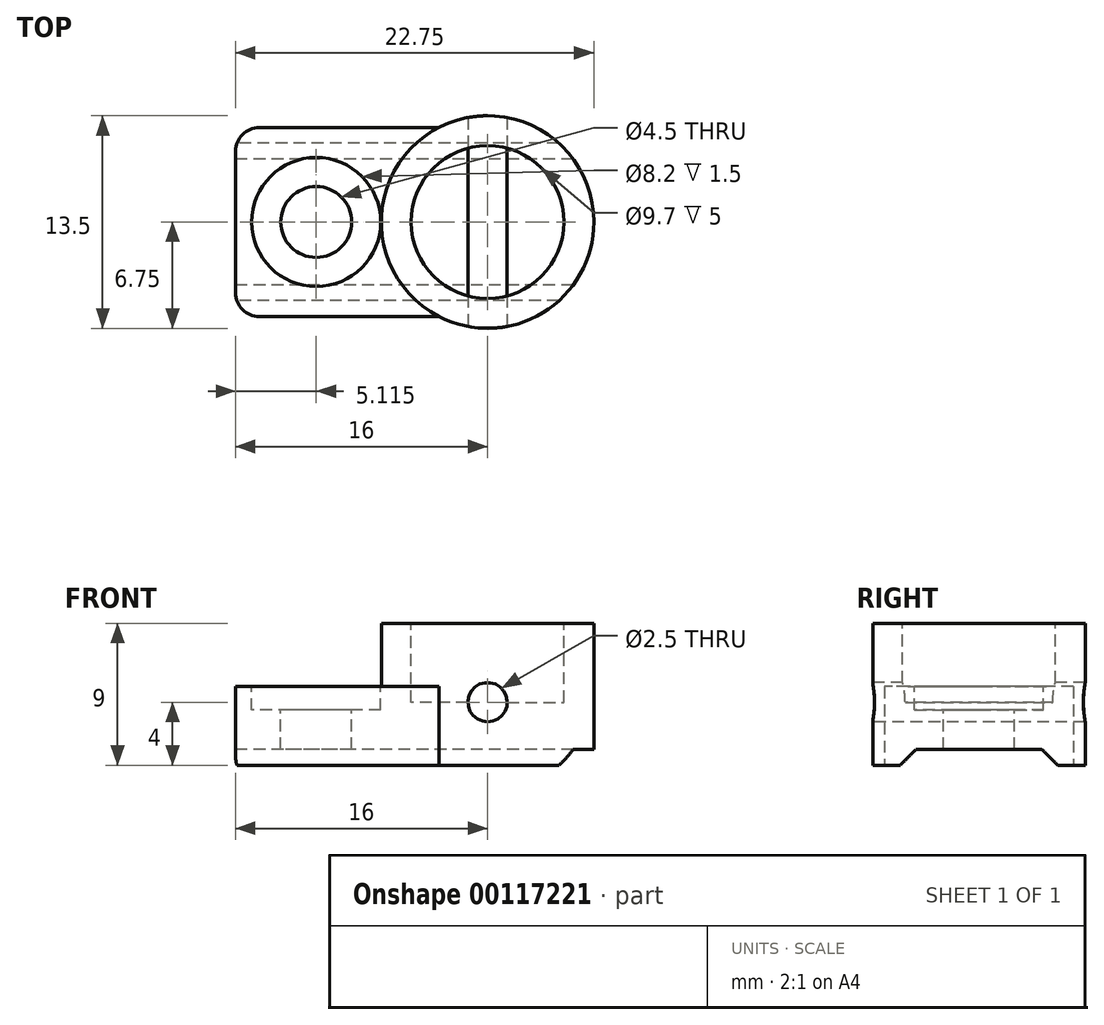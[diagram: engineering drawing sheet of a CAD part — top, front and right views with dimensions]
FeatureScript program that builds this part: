
annotation { "Feature Type Name" : "Feature", "Feature Type Description" : "" }
export const myFeature = defineFeature(function(context is Context, id is Id, definition is map)
    precondition{}
    {
        {
            var Q0;
            Q0=qCreatedBy(makeId("Top.planeOp"),FACE);
            var sketch = newSketch(context, id + "F0", { "sketchPlane" : qUnion([Q0])});
            skLineSegment(sketch, "E0.bottom", {"start": v(2.4, -6) * mm, "end": v(-10.5, -6) * mm});
            skLineSegment(sketch, "E0.right", {"start": v(-10.5, -6) * mm, "end": v(-10.5, 6) * mm});
            skPoint(sketch, "E0.middle", {"position": v(0, 0) * mm});
            skArc(sketch, "E1", {"start": v(2.4, -6) * mm, "mid": v(12.25, 0) * mm, "end": v(2.4, 6) * mm});
            skLineSegment(sketch, "E2.trimOffspring", {"start": v(2.4, 6) * mm, "end": v(-10.5, 6) * mm});
            skPoint(sketch, "E3.orphan", {"position": v(10.5, 6) * mm});
            skPoint(sketch, "E4.orphan", {"position": v(10.5, -6) * mm});
            skSolve(sketch);
        }
        {
            var Q0;
            Q0=makeQuery(id+"F0.imprint","IMPRINT",FACE,{"disambiguationData":[TD([[makeQuery(id+"F0.imprint","IMPRINT",EDGE,{"derivedFrom":sQuery(id+"F0.wireOp",EDGE,"E0.bottom")}),-1.0]])]});
            extrude(context, id + "F1", {"entities" : qUnion([Q0]), "depth" : 5 * mm});
        }
        {
            var Q0;
            Q0=makeQuery(id+"F1.opExtrude","SWEPT_FACE",FACE,{"disambiguationData":[OSD([sQuery(id+"F0.wireOp",EDGE,"E0.right")])]});
            var sketch = newSketch(context, id + "F2", { "sketchPlane" : qUnion([Q0])});
            skLineSegment(sketch, "E5.top", {"start": v(4, 1) * mm, "end": v(-4, 1) * mm});
            skPoint(sketch, "E5.middle", {"position": v(0, 0) * mm});
            skLineSegment(sketch, "E6", {"start": v(5.5, -0.5) * mm, "end": v(-5.5, -0.5) * mm});
            skLineSegment(sketch, "E7", {"start": v(4, 1) * mm, "end": v(5.5, -0.5) * mm});
            skLineSegment(sketch, "E8", {"start": v(-4, 1) * mm, "end": v(-5.5, -0.5) * mm});
            skSolve(sketch);
        }
        {
            var Q0;
            Q0=makeQuery(id+"F2.imprint","IMPRINT",FACE,{"disambiguationData":[TD([[makeQuery(id+"F2.imprint","IMPRINT",EDGE,{"derivedFrom":sQuery(id+"F2.wireOp",EDGE,"uNMLys3R-UcMP-iXmw-oIHl-g7IWJ4T2flMs.top")}),1.0]])]});
            var Q1;
            Q1=makeQuery(id+"F2.imprint","IMPRINT",FACE,{"disambiguationData":[TD([[makeQuery(id+"F2.imprint","IMPRINT",EDGE,{"derivedFrom":sQuery(id+"F2.wireOp",EDGE,"E5.top")}),1.0]])]});
            extrude(context, id + "F3", {"entities" : qUnion([Q0, Q1]), "operationType" : NewBodyOperationType.REMOVE, "endBound" : BoundingType.THROUGH_ALL, "oppositeDirection" : true, "depth" : 25 * mm});
        }
        {
            var Q0;
            Q0=makeQuery(id+"F1.opExtrude","CAP_FACE",FACE,{"disambiguationData":[OSD([sQuery(id+"F0.wireOp",EDGE,"E0.bottom"),sQuery(id+"F0.wireOp",EDGE,"E0.right"),sQuery(id+"F0.wireOp",EDGE,"E1"),sQuery(id+"F0.wireOp",EDGE,"E2.trimOffspring")])],"isStart":false});
            var sketch = newSketch(context, id + "F4", { "sketchPlane" : qUnion([Q0])});
            skLineSegment(sketch, "E9", {"start": v(-10.5, 0) * mm, "end": v(12.25, 0) * mm, "construction": true});
            skCircle(sketch, "E10", {"center": v(-5.38, 0) * mm, "radius": 2.25 * mm});
            skSolve(sketch);
        }
        {
            var Q0;
            Q0=makeQuery(id+"F4.imprint","IMPRINT",FACE,{"disambiguationData":[TD([[makeQuery(id+"F4.imprint","IMPRINT",EDGE,{"derivedFrom":sQuery(id+"F4.wireOp",EDGE,"E10")}),1.0]])]});
            extrude(context, id + "F5", {"entities" : qUnion([Q0]), "operationType" : NewBodyOperationType.REMOVE, "oppositeDirection" : true, "depth" : 25 * mm});
        }
        {
            var Q0;
            Q0=makeQuery(id+"F1.opExtrude","CAP_FACE",FACE,{"disambiguationData":[OSD([sQuery(id+"F0.wireOp",EDGE,"E0.bottom"),sQuery(id+"F0.wireOp",EDGE,"E0.right"),sQuery(id+"F0.wireOp",EDGE,"E1"),sQuery(id+"F0.wireOp",EDGE,"E2.trimOffspring")])],"isStart":false});
            var sketch = newSketch(context, id + "F6", { "sketchPlane" : qUnion([Q0])});
            skCircle(sketch, "E11", {"center": v(-5.38, 0) * mm, "radius": 4.1 * mm});
            skSolve(sketch);
        }
        {
            var Q0;
            Q0=makeQuery(id+"F6.imprint","IMPRINT",FACE,{"disambiguationData":[TD([[makeQuery(id+"F6.imprint","IMPRINT",EDGE,{"derivedFrom":sQuery(id+"F6.wireOp",EDGE,"E11")}),1.0]])]});
            extrude(context, id + "F7", {"entities" : qUnion([Q0]), "operationType" : NewBodyOperationType.REMOVE, "oppositeDirection" : true, "depth" : 1.5 * mm});
        }
        {
            var Q0;
            Q0=makeQuery(id+"F1.opExtrude","CAP_FACE",FACE,{"disambiguationData":[OSD([sQuery(id+"F0.wireOp",EDGE,"E0.bottom"),sQuery(id+"F0.wireOp",EDGE,"E0.right"),sQuery(id+"F0.wireOp",EDGE,"E1"),sQuery(id+"F0.wireOp",EDGE,"E2.trimOffspring")])],"isStart":false});
            var sketch = newSketch(context, id + "F8", { "sketchPlane" : qUnion([Q0])});
            skCircle(sketch, "E12", {"center": v(5.5, 0) * mm, "radius": 6.75 * mm});
            skSolve(sketch);
        }
        {
            var Q0;
            {var subQ0=sQuery(id+"F8.wireOp",EDGE,"E12");var subQ1=makeQuery(id+"F8.imprint","INTERSECT",VERTEX,{"derivedFrom":[makeQuery(id+"F1.opExtrude","CAP_EDGE",EDGE,{"disambiguationData":[OSD([sQuery(id+"F0.wireOp",EDGE,"E0.bottom")])],"isStart":false}),subQ0]});Q0=makeQuery(id+"F8.imprint","IMPRINT",FACE,{"disambiguationData":[TD([[makeQuery(id+"F8.imprint","IMPRINT",EDGE,{"disambiguationData":[TD([[subQ1,-1.0]])],"derivedFrom":subQ0}),1.0]])]});}
            extrude(context, id + "F9", {"entities" : qUnion([Q0]), "operationType" : NewBodyOperationType.ADD, "depth" : 4 * mm});
        }
        {
            var Q0;
            Q0=makeQuery(id+"F1.opExtrude","SWEPT_EDGE",EDGE,{"disambiguationData":[OSD([sQuery(id+"F0.wireOp",EDGE,"E0.bottom"),sQuery(id+"F0.wireOp",EDGE,"E0.right")])]});
            var Q1;
            Q1=makeQuery(id+"F1.opExtrude","SWEPT_EDGE",EDGE,{"disambiguationData":[OSD([sQuery(id+"F0.wireOp",EDGE,"E0.right"),sQuery(id+"F0.wireOp",EDGE,"E2.trimOffspring")])]});
            fillet(context, id + "F10", {"entities" : qUnion([Q0, Q1]), "radius" : 1.5 * mm, "tangentPropagation" : true, "allowEdgeOverflow" : false});
        }
        {
            var Q0;
            Q0=makeQuery(id+"F9.opExtrude","CAP_FACE",FACE,{"disambiguationData":[OSD([sQuery(id+"F8.wireOp",EDGE,"E12")])],"isStart":false});
            var sketch = newSketch(context, id + "F11", { "sketchPlane" : qUnion([Q0])});
            skCircle(sketch, "E13", {"center": v(5.5, 0) * mm, "radius": 4.85 * mm});
            skSolve(sketch);
        }
        {
            var Q0;
            Q0=makeQuery(id+"F11.imprint","IMPRINT",FACE,{"disambiguationData":[TD([[makeQuery(id+"F11.imprint","IMPRINT",EDGE,{"derivedFrom":sQuery(id+"F11.wireOp",EDGE,"E13")}),1.0]])]});
            extrude(context, id + "F12", {"entities" : qUnion([Q0]), "operationType" : NewBodyOperationType.REMOVE, "oppositeDirection" : true, "depth" : 5 * mm});
        }
        {
            var Q0;
            Q0=qCreatedBy(makeId("Front.planeOp"),FACE);
            var sketch = newSketch(context, id + "F13", { "sketchPlane" : qUnion([Q0])});
            skLineSegment(sketch, "E14", {"start": v(23.19, 4) * mm, "end": v(-33.3, 4) * mm, "construction": true});
            skLineSegment(sketch, "E15", {"start": v(5.5, 25.7) * mm, "end": v(5.5, -15.3) * mm, "construction": true});
            skCircle(sketch, "E16", {"center": v(5.5, 4) * mm, "radius": 1.25 * mm});
            skSolve(sketch);
        }
        {
            var Q0;
            Q0 = qSketchRegion(id + "F13", true);
            extrude(context, id + "F14", {"entities" : qUnion([Q0]), "operationType" : NewBodyOperationType.REMOVE, "endBound" : BoundingType.SYMMETRIC, "oppositeDirection" : true, "depth" : 25 * mm});
        }
    });
